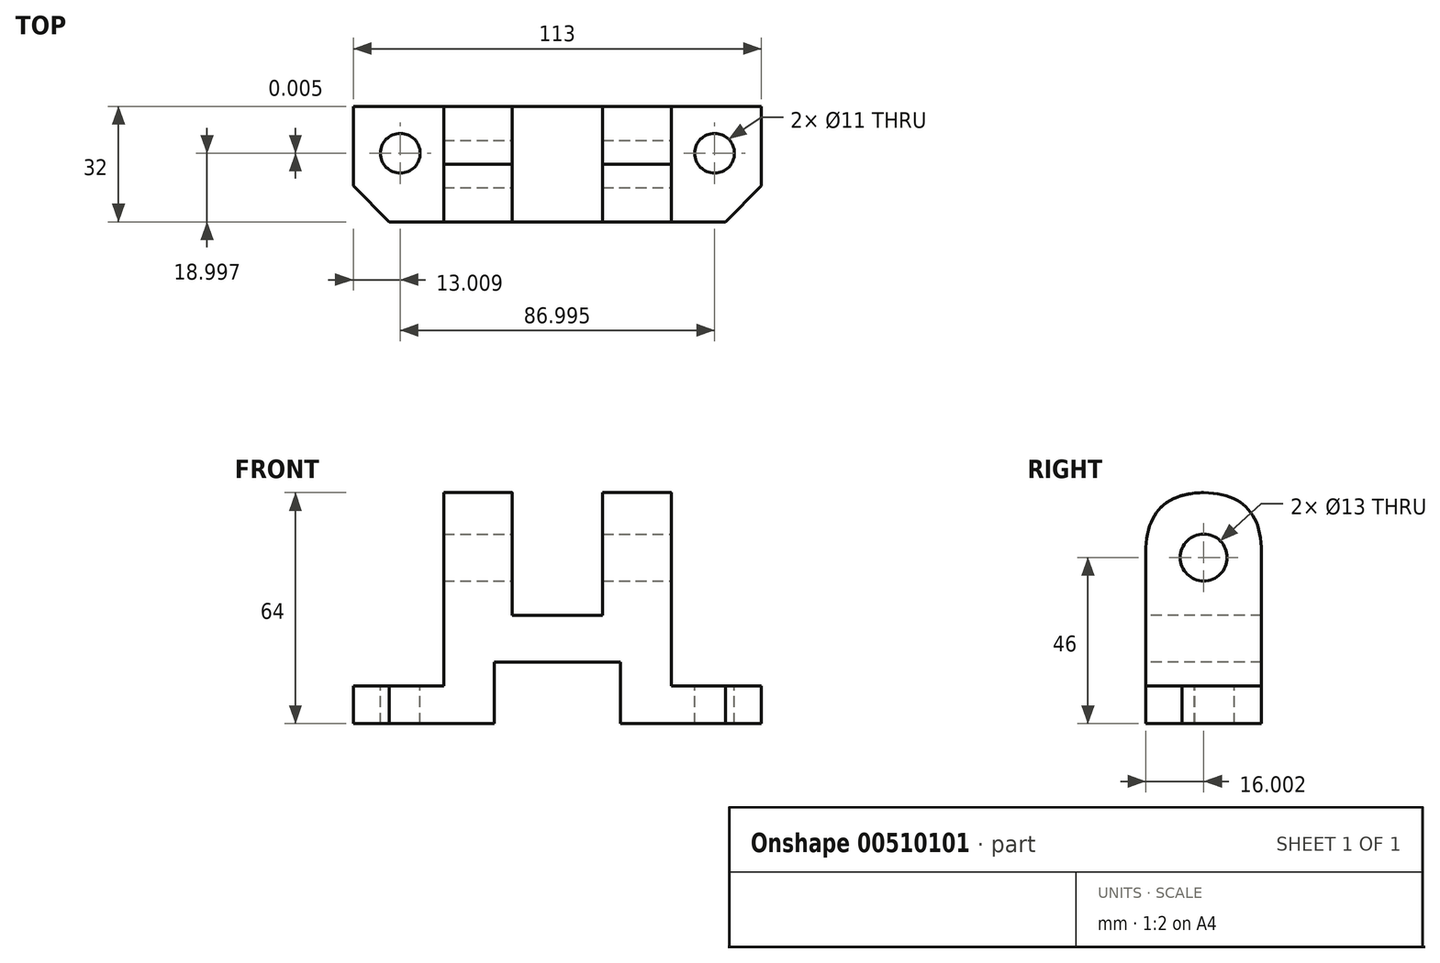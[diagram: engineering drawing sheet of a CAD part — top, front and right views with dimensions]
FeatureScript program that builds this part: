
annotation { "Feature Type Name" : "Feature", "Feature Type Description" : "" }
export const myFeature = defineFeature(function(context is Context, id is Id, definition is map)
    precondition{}
    {
        {
            var Q0;
            Q0=qCreatedBy(makeId("Top.planeOp"),FACE);
            var sketch = newSketch(context, id + "F0", { "sketchPlane" : qUnion([Q0])});
            skLineSegment(sketch, "E0.bottom", {"start": v(-83.48, -1.78) * mm, "end": v(29.52, -1.78) * mm});
            skLineSegment(sketch, "E0.top", {"start": v(-83.48, -33.78) * mm, "end": v(29.52, -33.78) * mm});
            skLineSegment(sketch, "E0.left", {"start": v(-83.48, -1.78) * mm, "end": v(-83.48, -33.78) * mm});
            skLineSegment(sketch, "E0.right", {"start": v(29.52, -1.78) * mm, "end": v(29.52, -33.78) * mm});
            skSolve(sketch);
        }
        {
            var Q0;
            Q0=makeQuery(id+"F0.imprint","IMPRINT",FACE,{"disambiguationData":[TD([[makeQuery(id+"F0.imprint","IMPRINT",EDGE,{"derivedFrom":sQuery(id+"F0.wireOp",EDGE,"E0.bottom")}),-1.0]])]});
            extrude(context, id + "F1", {"entities" : qUnion([Q0]), "depth" : 64 * mm});
        }
        {
            var Q0;
            Q0=makeQuery(id+"F1.opExtrude","CAP_FACE",FACE,{"disambiguationData":[OSD([sQuery(id+"F0.wireOp",EDGE,"E0.bottom"),sQuery(id+"F0.wireOp",EDGE,"E0.top"),sQuery(id+"F0.wireOp",EDGE,"E0.left"),sQuery(id+"F0.wireOp",EDGE,"E0.right")])],"isStart":false});
            var sketch = newSketch(context, id + "F2", { "sketchPlane" : qUnion([Q0])});
            skLineSegment(sketch, "E1.bottom", {"start": v(-83.48, -1.78) * mm, "end": v(-58.48, -1.78) * mm});
            skLineSegment(sketch, "E1.top", {"start": v(-83.48, -33.78) * mm, "end": v(-58.48, -33.78) * mm});
            skLineSegment(sketch, "E1.left", {"start": v(-83.48, -1.78) * mm, "end": v(-83.48, -33.78) * mm});
            skLineSegment(sketch, "E1.right", {"start": v(-58.48, -1.78) * mm, "end": v(-58.48, -33.78) * mm});
            skLineSegment(sketch, "E2.bottom", {"start": v(29.52, -1.78) * mm, "end": v(4.52, -1.78) * mm});
            skLineSegment(sketch, "E2.top", {"start": v(29.52, -33.78) * mm, "end": v(4.52, -33.78) * mm});
            skLineSegment(sketch, "E2.left", {"start": v(29.52, -1.78) * mm, "end": v(29.52, -33.78) * mm});
            skLineSegment(sketch, "E2.right", {"start": v(4.52, -1.78) * mm, "end": v(4.52, -33.78) * mm});
            skSolve(sketch);
        }
        {
            var Q0;
            Q0 = qSketchRegion(id + "F2", true);
            extrude(context, id + "F3", {"entities" : qUnion([Q0]), "operationType" : NewBodyOperationType.REMOVE, "oppositeDirection" : true, "depth" : 53.54 * mm});
        }
        {
            var Q0;
            Q0=makeQuery(id+"F1.opExtrude","SWEPT_FACE",FACE,{"disambiguationData":[OSD([sQuery(id+"F0.wireOp",EDGE,"E0.top")])]});
            var sketch = newSketch(context, id + "F4", { "sketchPlane" : qUnion([Q0])});
            skLineSegment(sketch, "E3.bottom", {"start": v(-44.48, 0) * mm, "end": v(-9.48, 0) * mm});
            skLineSegment(sketch, "E3.top", {"start": v(-44.48, 17) * mm, "end": v(-9.48, 17) * mm});
            skLineSegment(sketch, "E3.left", {"start": v(-44.48, 0) * mm, "end": v(-44.48, 17) * mm});
            skLineSegment(sketch, "E3.right", {"start": v(-9.48, 0) * mm, "end": v(-9.48, 17) * mm});
            skSolve(sketch);
        }
        {
            var Q0;
            Q0 = qSketchRegion(id + "F4", true);
            extrude(context, id + "F5", {"entities" : qUnion([Q0]), "operationType" : NewBodyOperationType.REMOVE, "oppositeDirection" : true, "depth" : 34.54 * mm});
        }
        {
            var Q0;
            Q0=makeQuery(id+"F1.opExtrude","SWEPT_EDGE",EDGE,{"disambiguationData":[OSD([sQuery(id+"F0.wireOp",EDGE,"E0.top"),sQuery(id+"F0.wireOp",EDGE,"E0.right")])]});
            var Q1;
            Q1=makeQuery(id+"F1.opExtrude","SWEPT_EDGE",EDGE,{"disambiguationData":[OSD([sQuery(id+"F0.wireOp",EDGE,"E0.top"),sQuery(id+"F0.wireOp",EDGE,"E0.left")])]});
            chamfer(context, id + "F6", {"entities" : qUnion([Q0, Q1]), "width" : 10 * mm, "tangentPropagation" : true});
        }
        {
            var Q0;
            Q0=makeQuery(id+"F1.opExtrude","SWEPT_FACE",FACE,{"disambiguationData":[OSD([sQuery(id+"F0.wireOp",EDGE,"E0.top")])]});
            var sketch = newSketch(context, id + "F7", { "sketchPlane" : qUnion([Q0])});
            skLineSegment(sketch, "E4.bottom", {"start": v(-39.48, 64) * mm, "end": v(-14.48, 64) * mm});
            skLineSegment(sketch, "E4.top", {"start": v(-39.48, 30) * mm, "end": v(-14.48, 30) * mm});
            skLineSegment(sketch, "E4.left", {"start": v(-39.48, 64) * mm, "end": v(-39.48, 30) * mm});
            skLineSegment(sketch, "E4.right", {"start": v(-14.48, 64) * mm, "end": v(-14.48, 30) * mm});
            skSolve(sketch);
        }
        {
            var Q0;
            Q0=makeQuery(id+"F7.imprint","IMPRINT",FACE,{"disambiguationData":[TD([[makeQuery(id+"F7.imprint","IMPRINT",EDGE,{"derivedFrom":sQuery(id+"F7.wireOp",EDGE,"E4.bottom")}),-1.0]])]});
            extrude(context, id + "F8", {"entities" : qUnion([Q0]), "operationType" : NewBodyOperationType.REMOVE, "oppositeDirection" : true, "depth" : 33.27 * mm});
        }
        {
            var Q0;
            Q0=makeQuery(id+"F3.boolean.opBoolean","COPY",FACE,{"derivedFrom":makeQuery(id+"F3.opExtrude","CAP_FACE",FACE,{"disambiguationData":[OSD([sQuery(id+"F2.wireOp",EDGE,"E2.bottom"),sQuery(id+"F2.wireOp",EDGE,"E2.top"),sQuery(id+"F2.wireOp",EDGE,"E2.left"),sQuery(id+"F2.wireOp",EDGE,"E2.right")])],"isStart":false})});
            var sketch = newSketch(context, id + "F9", { "sketchPlane" : qUnion([Q0])});
            skCircle(sketch, "E5", {"center": v(16.52, -14.78) * mm, "radius": 5.5 * mm});
            skCircle(sketch, "E6", {"center": v(-70.47, -14.78) * mm, "radius": 5.5 * mm});
            skSolve(sketch);
        }
        {
            var Q0;
            Q0=makeQuery(id+"F9.imprint","IMPRINT",FACE,{"disambiguationData":[TD([[makeQuery(id+"F9.imprint","IMPRINT",EDGE,{"derivedFrom":sQuery(id+"F9.wireOp",EDGE,"E6")}),1.0]])]});
            var Q1;
            Q1=makeQuery(id+"F9.imprint","IMPRINT",FACE,{"disambiguationData":[TD([[makeQuery(id+"F9.imprint","IMPRINT",EDGE,{"derivedFrom":sQuery(id+"F9.wireOp",EDGE,"E5")}),1.0]])]});
            extrude(context, id + "F10", {"entities" : qUnion([Q0, Q1]), "operationType" : NewBodyOperationType.REMOVE, "oppositeDirection" : true, "depth" : 25.4 * mm});
        }
        {
            var Q0;
            Q0=makeQuery(id+"F3.boolean.opBoolean","COPY",FACE,{"derivedFrom":makeQuery(id+"F3.opExtrude","SWEPT_FACE",FACE,{"disambiguationData":[OSD([sQuery(id+"F2.wireOp",EDGE,"E2.right")])]})});
            var sketch = newSketch(context, id + "F11", { "sketchPlane" : qUnion([Q0])});
            skCircle(sketch, "E7", {"center": v(-17.78, 46) * mm, "radius": 6.5 * mm});
            skSolve(sketch);
        }
        {
            var Q0;
            Q0=makeQuery(id+"F11.imprint","IMPRINT",FACE,{"disambiguationData":[TD([[makeQuery(id+"F11.imprint","IMPRINT",EDGE,{"derivedFrom":sQuery(id+"F11.wireOp",EDGE,"E7")}),1.0]])]});
            extrude(context, id + "F12", {"entities" : qUnion([Q0]), "operationType" : NewBodyOperationType.REMOVE, "oppositeDirection" : true, "depth" : 82.3 * mm});
        }
        {
            var Q0;
            {var subQ0=sQuery(id+"F0.wireOp",EDGE,"E0.top");Q0=makeQuery(id+"F8.boolean.opBoolean","SPLIT",EDGE,{"disambiguationData":[TD([makeQuery(id+"F3.boolean.opBoolean","COPY",FACE,{"derivedFrom":makeQuery(id+"F3.opExtrude","SWEPT_FACE",FACE,{"disambiguationData":[OSD([sQuery(id+"F2.wireOp",EDGE,"E2.right")])]})})])],"derivedFrom":makeQuery(id+"F1.opExtrude","CAP_EDGE",EDGE,{"disambiguationData":[OSD([subQ0])],"isStart":false})});}
            var Q1;
            {var subQ0=sQuery(id+"F0.wireOp",EDGE,"E0.bottom");Q1=makeQuery(id+"F8.boolean.opBoolean","SPLIT",EDGE,{"disambiguationData":[TD([makeQuery(id+"F3.boolean.opBoolean","COPY",FACE,{"derivedFrom":makeQuery(id+"F3.opExtrude","SWEPT_FACE",FACE,{"disambiguationData":[OSD([sQuery(id+"F2.wireOp",EDGE,"E2.right")])]})})])],"derivedFrom":makeQuery(id+"F1.opExtrude","CAP_EDGE",EDGE,{"disambiguationData":[OSD([subQ0])],"isStart":false})});}
            var Q2;
            {var subQ0=sQuery(id+"F0.wireOp",EDGE,"E0.top");Q2=makeQuery(id+"F8.boolean.opBoolean","SPLIT",EDGE,{"disambiguationData":[TD([makeQuery(id+"F3.boolean.opBoolean","COPY",FACE,{"derivedFrom":makeQuery(id+"F3.opExtrude","SWEPT_FACE",FACE,{"disambiguationData":[OSD([sQuery(id+"F2.wireOp",EDGE,"E1.right")])]})})])],"derivedFrom":makeQuery(id+"F1.opExtrude","CAP_EDGE",EDGE,{"disambiguationData":[OSD([subQ0])],"isStart":false})});}
            var Q3;
            {var subQ0=sQuery(id+"F0.wireOp",EDGE,"E0.bottom");Q3=makeQuery(id+"F8.boolean.opBoolean","SPLIT",EDGE,{"disambiguationData":[TD([makeQuery(id+"F3.boolean.opBoolean","COPY",FACE,{"derivedFrom":makeQuery(id+"F3.opExtrude","SWEPT_FACE",FACE,{"disambiguationData":[OSD([sQuery(id+"F2.wireOp",EDGE,"E1.right")])]})})])],"derivedFrom":makeQuery(id+"F1.opExtrude","CAP_EDGE",EDGE,{"disambiguationData":[OSD([subQ0])],"isStart":false})});}
            fillet(context, id + "F13", {"entities" : qUnion([Q0, Q1, Q2, Q3]), "radius" : 16.56 * mm, "tangentPropagation" : true, "rho" : .5, "crossSection" : FilletCrossSection.CONIC, "allowEdgeOverflow" : false});
        }
    });
